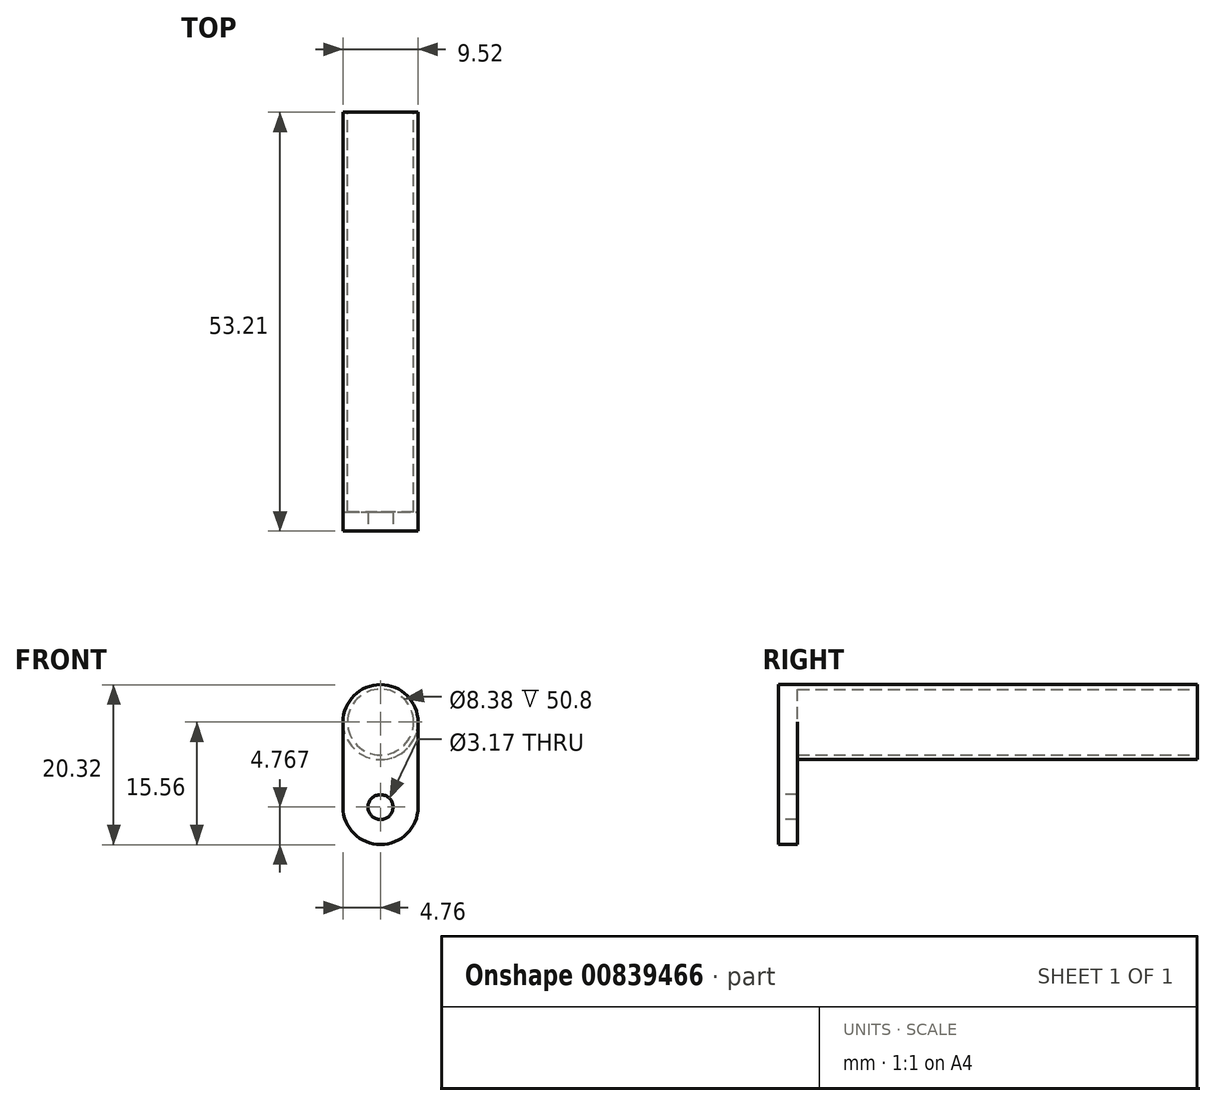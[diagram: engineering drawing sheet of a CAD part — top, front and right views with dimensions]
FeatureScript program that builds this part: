
annotation { "Feature Type Name" : "Feature", "Feature Type Description" : "" }
export const myFeature = defineFeature(function(context is Context, id is Id, definition is map)
    precondition{}
    {
        {
            var Q0;
            Q0=qCreatedBy(makeId("Front.planeOp"),FACE);
            var sketch = newSketch(context, id + "F0", { "sketchPlane" : qUnion([Q0])});
            skCircle(sketch, "E0", {"center": v(0, 0) * mm, "radius": 4.76 * mm});
            skCircle(sketch, "E1", {"center": v(0, 0) * mm, "radius": 4.19 * mm});
            skSolve(sketch);
        }
        {
            var Q0;
            Q0 = qSketchRegion(id + "F0", true);
            extrude(context, id + "F1", {"entities" : qUnion([Q0]), "depth" : 50.8 * mm, "offsetDistance" : 25.4 * mm});
        }
        {
            var Q0;
            Q0=makeQuery(id+"F1.opExtrude","CAP_FACE",FACE,{"disambiguationData":[OSD([sQuery(id+"F0.wireOp",EDGE,"E0"),sQuery(id+"F0.wireOp",EDGE,"E1")])],"isStart":false});
            var sketch = newSketch(context, id + "F2", { "sketchPlane" : qUnion([Q0])});
            skArc(sketch, "E2", {"start": v(4.76, 0) * mm, "mid": v(0, 4.76) * mm, "end": v(-4.76, 0) * mm});
            skArc(sketch, "E3", {"start": v(-4.76, -10.8) * mm, "mid": v(0, -15.56) * mm, "end": v(4.76, -10.8) * mm});
            skLineSegment(sketch, "E4", {"start": v(4.76, 0) * mm, "end": v(4.76, -10.8) * mm});
            skLineSegment(sketch, "E5", {"start": v(-4.76, 0) * mm, "end": v(-4.76, -10.8) * mm});
            skSolve(sketch);
        }
        {
            var Q0;
            Q0 = qSketchRegion(id + "F2", true);
            extrude(context, id + "F3", {"entities" : qUnion([Q0]), "operationType" : NewBodyOperationType.ADD, "depth" : 2.41 * mm, "offsetDistance" : 25.4 * mm});
        }
        {
            var Q0;
            Q0=makeQuery(id+"F3.opExtrude","CAP_FACE",FACE,{"disambiguationData":[OSD([sQuery(id+"F2.wireOp",EDGE,"E2"),sQuery(id+"F2.wireOp",EDGE,"E3"),sQuery(id+"F2.wireOp",EDGE,"E4"),sQuery(id+"F2.wireOp",EDGE,"E5")])],"isStart":false});
            var sketch = newSketch(context, id + "F4", { "sketchPlane" : qUnion([Q0])});
            skCircle(sketch, "E6", {"center": v(0, -10.8) * mm, "radius": 1.59 * mm});
            skSolve(sketch);
        }
        {
            var Q0;
            Q0 = qSketchRegion(id + "F4", true);
            extrude(context, id + "F5", {"entities" : qUnion([Q0]), "operationType" : NewBodyOperationType.REMOVE, "endBound" : BoundingType.THROUGH_ALL, "oppositeDirection" : true, "depth" : 25.4 * mm, "offsetDistance" : 25.4 * mm});
        }
    });
